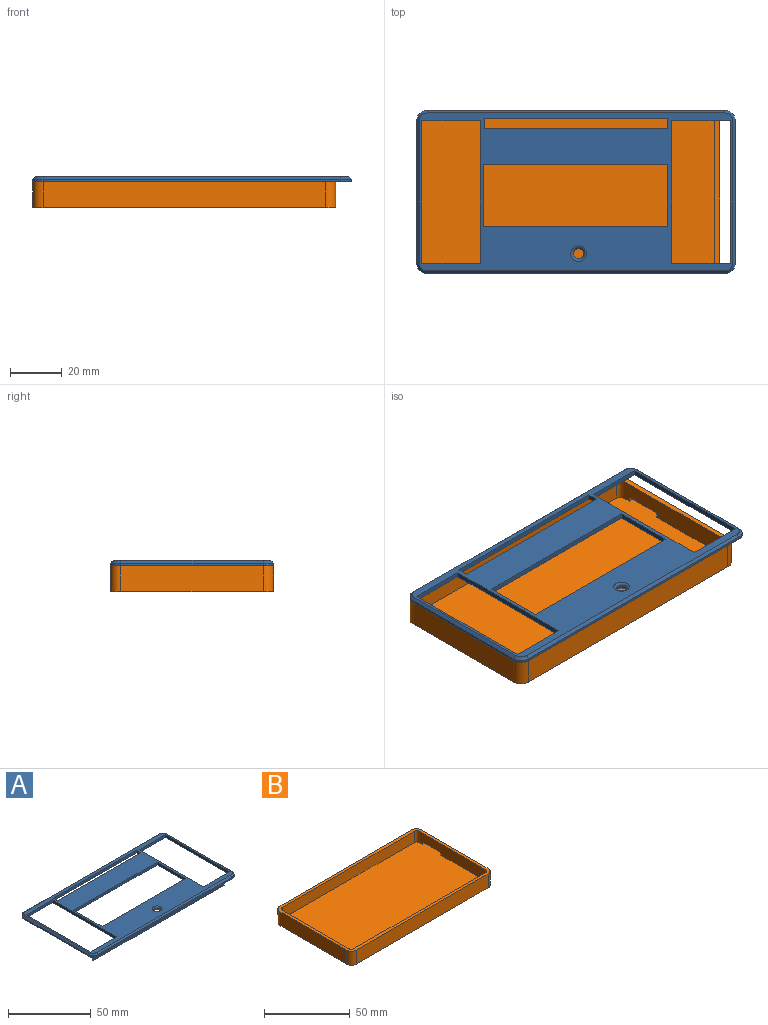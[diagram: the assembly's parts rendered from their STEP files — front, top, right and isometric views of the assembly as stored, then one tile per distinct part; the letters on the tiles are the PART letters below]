
ASSEMBLY  parts=2 mates=1
PART A: 45 faces, bbox 123x63x7 mm
  f0: plane 123x63mm, normal (0,0,-1), area 3080mm2, adj f2,f3,f4,f5,f6,f7,f8,f9
  f1: plane 121x61mm, normal (0,0,1), area 2866.5mm2, adj f10,f11,f12,f13,f14,f15,f16,f17
  f2: plane 55x1mm, normal (-1,0,0), area 55mm2, adj f0,f6,f9,f21
  f3: plane 115x1mm, normal (0,-1,0), area 115mm2, adj f0,f6,f7,f18
  f4: plane 55x1mm, normal (1,0,0), area 55mm2, adj f0,f7,f8,f22
  f5: plane 115x1mm, normal (0,1,0), area 115mm2, adj f0,f8,f9,f25
  f6: cylinder r=4mm len=4mm, axis (0,0,1), area 6.3mm2, adj f0,f2,f3,f19
  f7: cylinder r=4mm len=4mm, axis (0,0,-1), area 6.3mm2, adj f0,f3,f4,f20
  f8: cylinder r=4mm len=4mm, axis (0,0,1), area 6.3mm2, adj f0,f4,f5,f24
  f9: cylinder r=4mm len=4mm, axis (0,0,-1), area 6.3mm2, adj f0,f2,f5,f23
  f10: plane 22.5x2mm, normal (0,-1,0), area 45mm2, adj f0,f1,f11,f13
  f11: plane 55x2mm, normal (1,0,0), area 110mm2, adj f0,f1,f10,f12,f37
  f12: plane 22.5x2mm, normal (0,1,0), area 45mm2, adj f0,f1,f11,f13,f30
  f13: plane 55x2mm, normal (-1,0,0), area 110mm2, adj f0,f1,f10,f12
  f14: plane 22.5x2mm, normal (0,-1,0), area 45mm2, adj f0,f1,f15,f17
  f15: plane 55x2mm, normal (1,0,0), area 110mm2, adj f0,f1,f14,f16
  f16: plane 22.5x2mm, normal (0,1,0), area 45mm2, adj f0,f1,f15,f17,f34
  f17: plane 55x2mm, normal (-1,0,0), area 110mm2, adj f0,f1,f14,f16,f35
  f18: plane 115x1mm, normal (0,-0.71,0.71), area 162.6mm2, adj f1,f3,f19,f20
  f19: cone r=3mm half-angle=45deg, axis (0,0,-1), area 7.8mm2, adj f1,f6,f18,f21
  f20: cone r=3mm half-angle=45deg, axis (0,0,-1), area 7.8mm2, adj f1,f7,f18,f22
  f21: plane 55x1mm, normal (-0.71,0,0.71), area 77.8mm2, adj f1,f2,f19,f23
  f22: plane 55x1mm, normal (0.71,0,0.71), area 77.8mm2, adj f1,f4,f20,f24
  f23: cone r=3mm half-angle=45deg, axis (0,0,-1), area 7.8mm2, adj f1,f9,f21,f25
  f24: cone r=3mm half-angle=45deg, axis (0,0,-1), area 7.8mm2, adj f1,f8,f22,f25
  f25: plane 115x1mm, normal (0,0.71,0.71), area 162.6mm2, adj f1,f5,f23,f24
  f26: plane 71.2x2mm, normal (0,-1,0), area 142.4mm2, adj f0,f1,f27,f29
  f27: plane 24.15x2mm, normal (1,0,0), area 48.3mm2, adj f0,f1,f26,f28
  f28: plane 71.2x2mm, normal (0,1,0), area 142.4mm2, adj f0,f1,f27,f29
  f29: plane 24.15x2mm, normal (-1,0,0), area 48.3mm2, adj f0,f1,f26,f28
  f30: plane 17.76x5mm, normal (0,1,-0.05), area 87.6mm2, adj f12,f31,f37,f38
  f31: plane 5x0.8mm, normal (1,0,-0.05), area 2.7mm2, adj f0,f30,f32,f38
  f32: plane 112.8x5mm, normal (0,-1,-0.05), area 563.5mm2, adj f0,f31,f33,f38
  f33: plane 5x0.8mm, normal (-1,0,-0.05), area 2.7mm2, adj f0,f32,f34,f38
  f34: plane 21.56x5mm, normal (0,1,-0.05), area 106.6mm2, adj f16,f33,f35,f38
  f35: plane 5x1.26mm, normal (-1,0,-0.05), area 5mm2, adj f17,f34,f36,f38
  f36: plane 74x5mm, normal (0,1,-0.05), area 369.2mm2, adj f0,f35,f37,f38
  f37: plane 5x1.26mm, normal (1,0,-0.05), area 5mm2, adj f11,f30,f36,f38
  f38: plane 112.28x1.28mm, normal (0,0,-1), area 104.5mm2, adj f30,f31,f32,f33,f34,f35,f36,f37
  f39: plane 71x2mm, normal (0,1,0), area 142mm2, adj f0,f1,f40,f42
  f40: plane 4x2mm, normal (-1,0,0), area 8mm2, adj f0,f1,f39,f41
  f41: plane 71x2mm, normal (0,-1,0), area 142mm2, adj f0,f1,f40,f42
  f42: plane 4x2mm, normal (1,0,0), area 8mm2, adj f0,f1,f39,f41
  f43: cylinder r=2mm len=4mm, axis (0,0,1), area 12.6mm2, adj f0,f44
  f44: torus R=3mm, axis (0,0,1), area 23.3mm2, adj f1,f43
PART B: 22 faces, bbox 117x63x10 mm
  f0: plane 55x10mm, normal (1,0,0), area 520mm2, adj f1,f5,f8,f9,f14,f19,f20,f21
  f1: plane 117x63mm, normal (0,0,1), area 693.7mm2, adj f0,f2,f3,f4,f6,f7,f8,f9
  f2: plane 109x10mm, normal (0,1,0), area 1090mm2, adj f1,f5,f6,f9
  f3: plane 55x10mm, normal (-1,0,0), area 550mm2, adj f1,f5,f6,f7
  f4: plane 109x10mm, normal (0,-1,0), area 1090mm2, adj f1,f5,f7,f8
  f5: plane 117x63mm, normal (0,0,-1), area 7357.3mm2, adj f0,f2,f3,f4,f6,f7,f8,f9
  f6: cylinder r=4mm len=10mm, axis (0,0,-1), area 62.8mm2, adj f1,f2,f3,f5
  f7: cylinder r=4mm len=10mm, axis (0,0,1), area 62.8mm2, adj f1,f3,f4,f5
  f8: cylinder r=4mm len=10mm, axis (0,0,-1), area 62.8mm2, adj f0,f1,f4,f5
  f9: cylinder r=4mm len=10mm, axis (0,0,1), area 62.8mm2, adj f0,f1,f2,f5
  f10: plane 109x8mm, normal (0,-1,0), area 872mm2, adj f1,f14,f15,f18
  f11: plane 55x8mm, normal (1,0,0), area 440mm2, adj f1,f14,f15,f16
  f12: plane 109x8mm, normal (0,1,0), area 872mm2, adj f1,f14,f16,f17
  f13: plane 55x8mm, normal (-1,0,0), area 410mm2, adj f1,f14,f17,f18,f19,f20,f21
  f14: plane 115x59mm, normal (0,0,1), area 6693.6mm2, adj f0,f10,f11,f12,f13,f15,f16,f17
  f15: cylinder r=2mm len=8mm, axis (0,0,-1), area 25.1mm2, adj f1,f10,f11,f14
  f16: cylinder r=2mm len=8mm, axis (0,0,1), area 25.1mm2, adj f1,f11,f12,f14
  f17: cylinder r=2mm len=8mm, axis (0,0,-1), area 25.1mm2, adj f1,f12,f13,f14
  f18: cylinder r=2mm len=8mm, axis (0,0,1), area 25.1mm2, adj f1,f10,f13,f14
  f19: plane 15x2mm, normal (0,0,-1), area 30mm2, adj f0,f13,f20,f21
  f20: plane 2x2mm, normal (0,1,0), area 4mm2, adj f0,f13,f14,f19
  f21: plane 2x2mm, normal (0,-1,0), area 4mm2, adj f0,f13,f14,f19
PLACE A t=(22.57,24.67,7.3)mm
PLACE B t=(20.98,6.13,7.3)mm
MATE planar A.f0 <-> B.f1  axis (0,0,-1) through (33.38,25.03,7.3)mm
